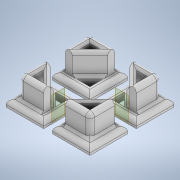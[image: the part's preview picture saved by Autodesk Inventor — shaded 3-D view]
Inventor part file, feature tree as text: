
AUTODESK INVENTOR PART (.ipt)
format: ipt  version: 2021 (Build 250183000, 183)  size: 257,024 bytes
history: native  units: mm
features: extrude x3, fillet x3, sketch x3, chamfer x2, plane x2, mirror x2, other x1
ambient origin geometry x8: Origin, YZ Plane, XZ Plane, XY Plane, X Axis, Y Axis, Z Axis, Center Point
bodies: Body1 (feature_tree)
feature tree (16):
  other  "Sólido1"
  extrude  "Extrusión1"  Depth=3.0mm
  extrude  "Extrusión2"  Depth=10.0mm
  chamfer  "Chaflán1"  Distance=3.0mm
  fillet  "Empalme1"  Radius=3.0mm
  chamfer  "Chaflán2"  Distance=3.0mm
  extrude  "Extrusión3"  Depth=2.0mm TaperAngle=45.0deg
  fillet  "Empalme2"  Radius=2.0mm
  fillet  "Empalme3"  Radius=2.0mm
  plane  "Plano de trabajo1"
  plane  "Plano de trabajo2"
  mirror  "Simetría1"
  mirror  "Simetría2"
  sketch  "Boceto1"  dims[d2=3.0mm d4=3.0mm]
  sketch  "Boceto2"  dims[d6=10.0mm d7=0.0mm d8=3.0mm]
  sketch  "Boceto4"  dims[d9=3.0mm d10=3.0mm d11=3.0mm d12=3.0mm d13=0.0mm d14=1.0mm d15=2.0mm d16=45.0deg d17=2.0mm d18=1.0mm d19=2.0mm d20=45.0deg d21=1.0mm d22=19.0mm d23=0.0mm d24=2.0mm d25=2.0mm d26=5.0mm d27=5.0mm]
